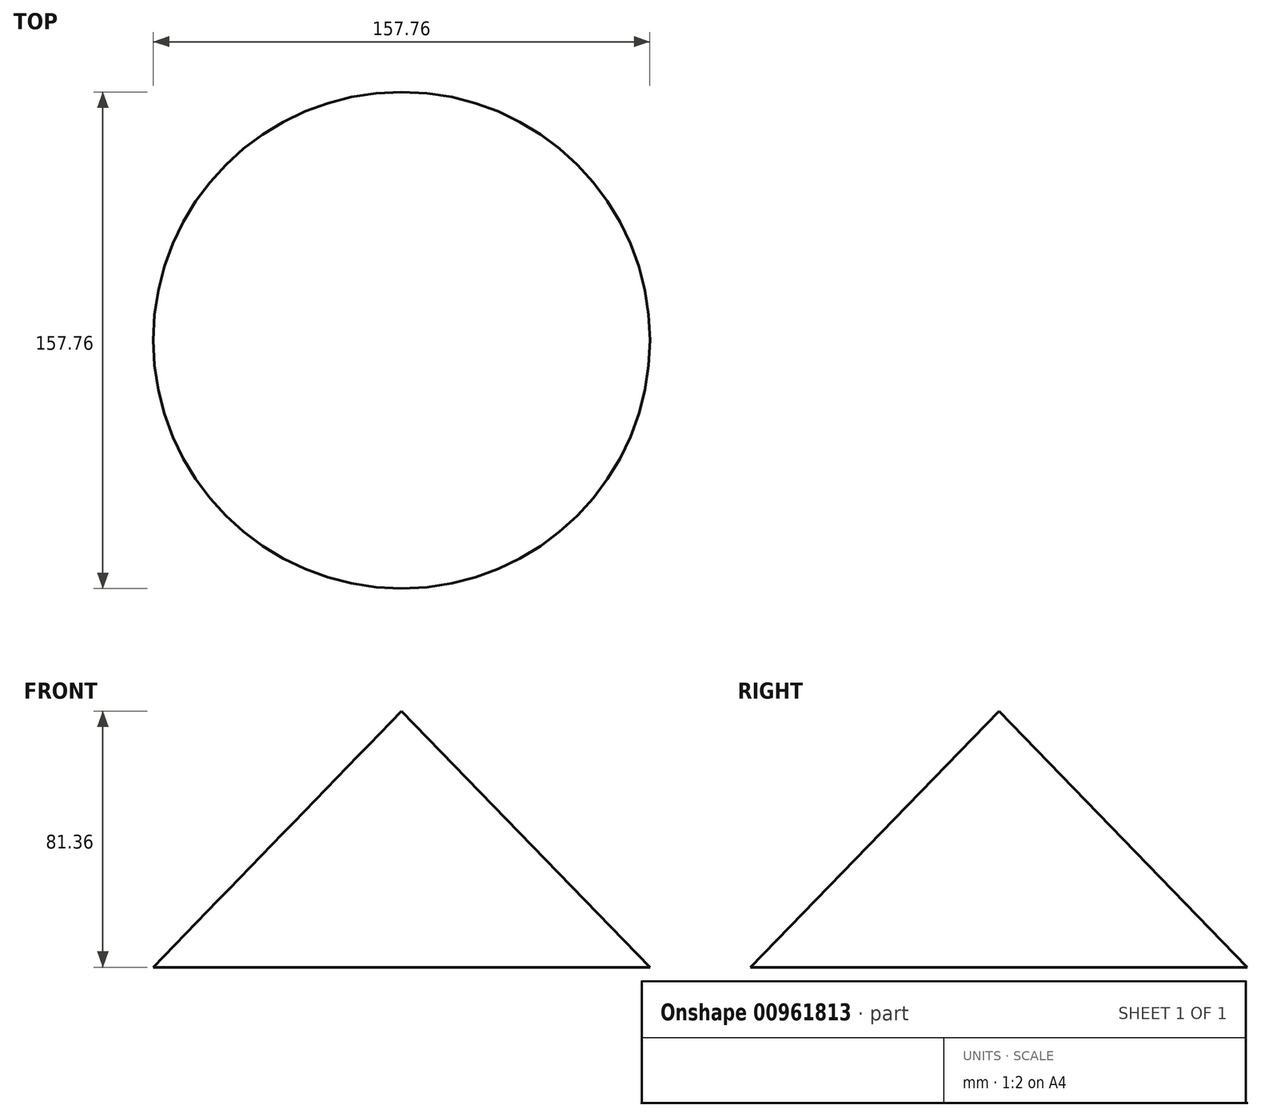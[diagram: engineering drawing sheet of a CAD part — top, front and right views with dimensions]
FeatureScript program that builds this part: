
annotation { "Feature Type Name" : "Feature", "Feature Type Description" : "" }
export const myFeature = defineFeature(function(context is Context, id is Id, definition is map)
    precondition{}
    {
        {
            var Q0;
            Q0=qCreatedBy(makeId("Front.planeOp"),FACE);
            var sketch = newSketch(context, id + "F0", { "sketchPlane" : qUnion([Q0])});
            skLineSegment(sketch, "E0", {"start": v(0, 0) * mm, "end": v(0, 81.36) * mm});
            skLineSegment(sketch, "E1", {"start": v(0, 81.36) * mm, "end": v(78.88, 0) * mm});
            skLineSegment(sketch, "E2", {"start": v(78.88, 0) * mm, "end": v(0, 0) * mm});
            skSolve(sketch);
        }
        {
            var Q0;
            Q0=makeQuery(id+"F0.imprint","IMPRINT",FACE,{"disambiguationData":[TD([[makeQuery(id+"F0.imprint","IMPRINT",EDGE,{"derivedFrom":sQuery(id+"F0.wireOp",EDGE,"E0")}),-1.0]])]});
            var Q1;
            Q1=sQuery(id+"F0.wireOp",EDGE,"E0");
            revolve(context, id + "F1", {"surfaceOperationType" : NewSurfaceOperationType.NEW, "entities" : qUnion([Q0]), "axis" : qUnion([Q1]), "revolveType" : RevolveType.FULL});
        }
    });
